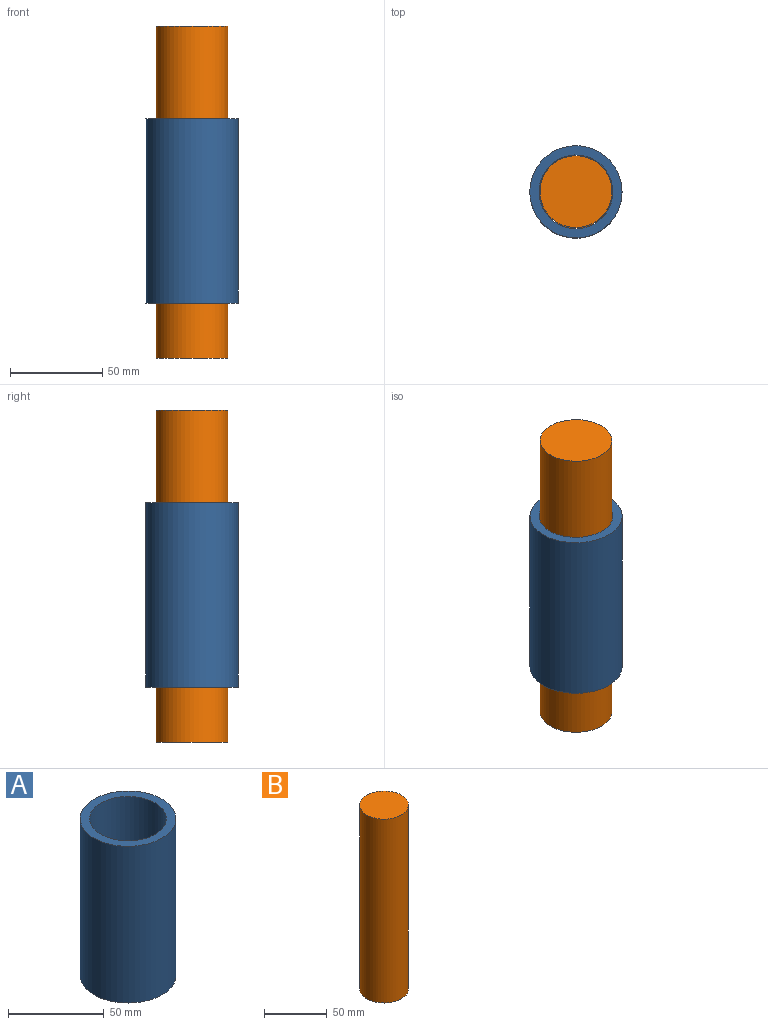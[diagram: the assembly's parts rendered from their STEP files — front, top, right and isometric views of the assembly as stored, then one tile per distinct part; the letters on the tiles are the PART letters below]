
ASSEMBLY  parts=2 mates=1
PART A: 4 faces, bbox 50x50x100 mm
  f0: cylinder r=25mm len=100mm, axis (0,0,-1), area 15708mm2, adj f1,f2
  f1: plane 50x50mm, normal (0,0,1), area 706.9mm2, adj f0,f3
  f2: plane 50x50mm, normal (0,0,-1), area 706.9mm2, adj f0,f3
  f3: cylinder r=20mm len=100mm, axis (0,0,1), area 12566.4mm2, adj f1,f2
PART B: 3 faces, bbox 39x39x180 mm
  f0: cylinder r=19.5mm len=180mm, axis (0,0,-1), area 22054mm2, adj f1,f2
  f1: plane 39x39mm, normal (0,0,1), area 1194.6mm2, adj f0
  f2: plane 39x39mm, normal (0,0,-1), area 1194.6mm2, adj f0
PLACE A t=(-85.37,46.14,7.62)mm
PLACE B t=(-85.37,46.14,-22.18)mm
MATE slider B.f0 <-> A.f3  axis (0,0,-1) through (-85.37,46.14,157.82)mm
